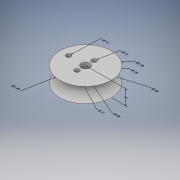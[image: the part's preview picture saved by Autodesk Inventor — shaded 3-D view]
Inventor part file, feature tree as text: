
AUTODESK INVENTOR PART (.ipt)
format: ipt  version: 2018 (Build 220112000, 112)  size: 164,352 bytes
history: native  units: in
note: dims shown in document units (in); Inventor stores cm internally (conversion verified against a paired STEP export)
features: other x10, sketch x6, hole x4, extrude x2, draft x2
ambient origin geometry x8: Origin, YZ Plane, XZ Plane, XY Plane, X Axis, Y Axis, Z Axis, Center Point
bodies: Solid1 (feature_tree)
feature tree (24):
  other  "Annotations"
  extrude  "Extrusion1"  Depth=0.175in TaperAngle=0.0deg
  draft  "FaceDraft1"
  extrude  "Extrusion2"  Depth=0.175in TaperAngle=0.0deg
  draft  "FaceDraft2"
  hole  "Hole1"  [1 undecoded]
  hole  "Hole2"  [1 undecoded]
  hole  "Hole4"  [1 undecoded]
  hole  "Hole5"  [1 undecoded]
  sketch  "Sketch1"  dims[d0=1.2in d1=0.175in d2=0.0in]
  sketch  "Sketch2"  dims[d3=60.0deg d4=0.175in d5=0.0in]
  sketch  "Sketch3"  dims[d6=60.0deg]
  sketch  "Sketch4"  dims[d7=0.2in d8=0.75in d9=0.375in d10=0.25in d11=0.5635in d12=1.0in d13=0.8108in d14=0.3in]
  sketch  "Sketch6"  dims[d15=0.11in d16=0.75in d17=0.375in d18=0.25in d19=0.5635in d20=1.0in d21=0.8108in d29=0.2in]
  sketch  "Sketch7"  dims[d30=0.11in d31=0.75in d32=0.375in d33=0.25in d34=0.5635in d35=1.0in d36=0.8108in d37=0.2in d38=0.11in d39=0.75in d40=0.375in d41=0.25in d42=0.5635in d43=1.0in d44=0.8108in d45=1.6099in d46=1.2in d51=0.35in d52=2.2188in d53=0.0636in d54=0.3622in d55=0.2in d56=2.0404in d57=0.11in d58=1.8002in d59=0.11in d60=0.1877in d61=0.0636in d62=0.3679in d63=0.11in d64=1.3977in d65=0.5938in d66=0.5436in d67=1.2in d68=2.3885in d69=0.0461in d70=0.315in d71=0.2in]
  other  "Diameter Dimension 1"
  other  "Linear Dimension 1"
  other  "Diameter Dimension 3"
  other  "Diameter Dimension 4"
  other  "Diameter Dimension 5"
  other  "Diameter Dimension 6"
  other  "Diameter Dimension 7"
  other  "Diameter Dimension 8"
  other  "Diameter Dimension 9"
note: 4 required parameter values undecoded (feature->parameter linkage not recoverable at this tier; creation-order binding heuristic only, values carry confidence <= 0.55)
